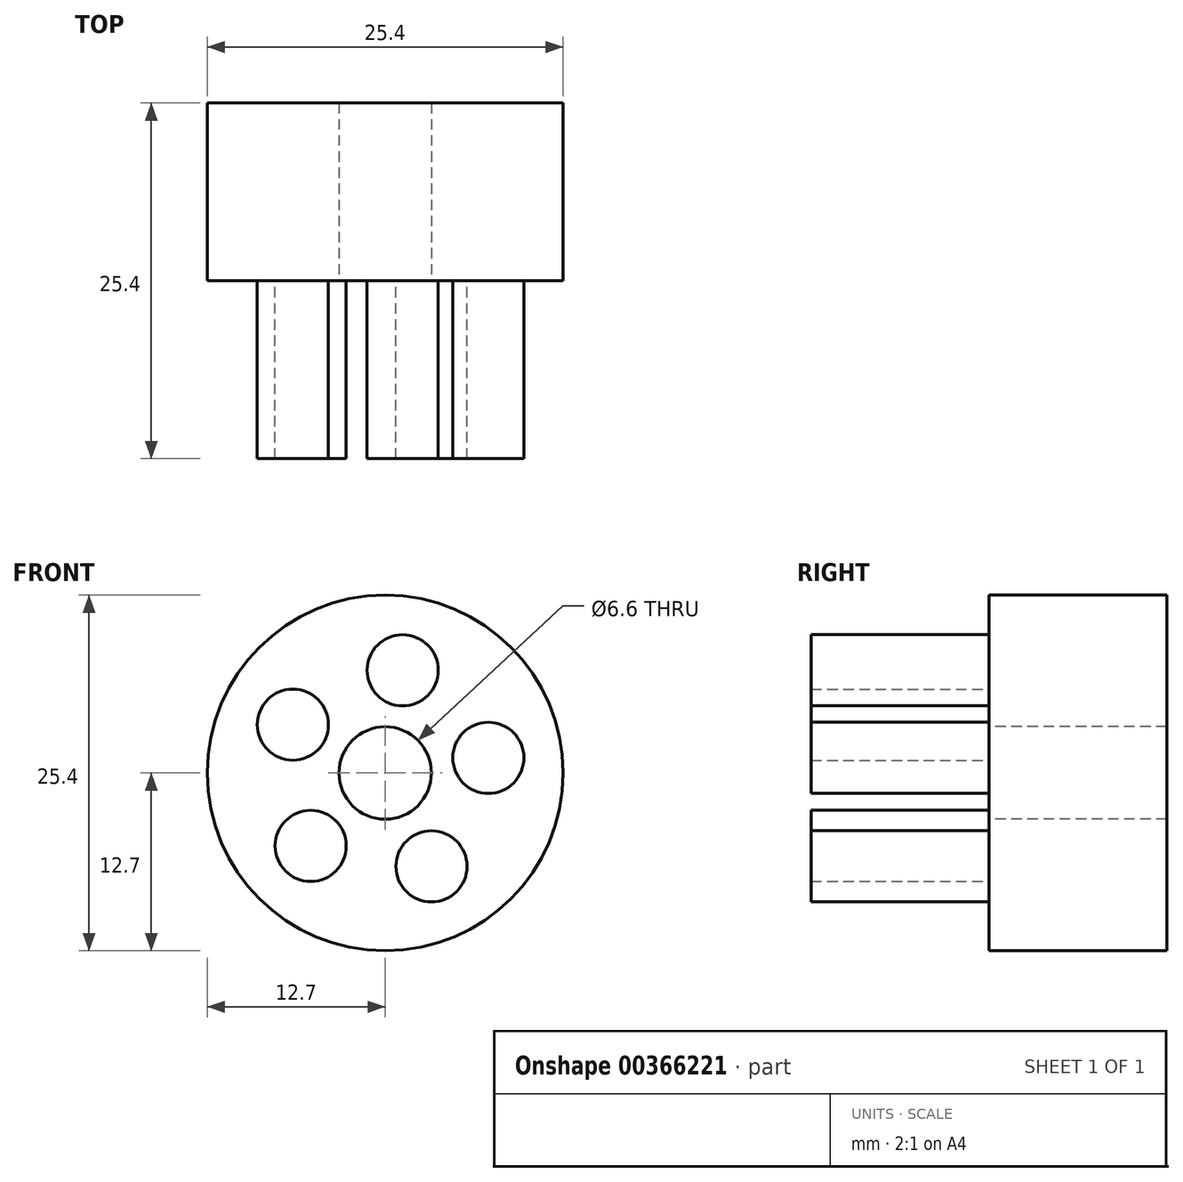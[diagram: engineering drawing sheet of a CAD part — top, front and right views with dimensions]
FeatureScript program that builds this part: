
annotation { "Feature Type Name" : "Feature", "Feature Type Description" : "" }
export const myFeature = defineFeature(function(context is Context, id is Id, definition is map)
    precondition{}
    {
        {
            var Q0;
            Q0=qCreatedBy(makeId("Front.planeOp"),FACE);
            var sketch = newSketch(context, id + "F0", { "sketchPlane" : qUnion([Q0])});
            skCircle(sketch, "E0", {"center": v(0, 0) * mm, "radius": 12.7 * mm});
            skSolve(sketch);
        }
        {
            var Q0;
            Q0 = qSketchRegion(id + "F0", true);
            var Q1;
            Q1=makeQuery(id+"F0.imprint","IMPRINT",FACE,{"disambiguationData":[TD([[makeQuery(id+"F0.imprint","IMPRINT",EDGE,{"derivedFrom":sQuery(id+"F0.wireOp",EDGE,"E0")}),1.0]])]});
            extrude(context, id + "F1", {"entities" : qUnion([Q0, Q1]), "depth" : 12.7 * mm});
        }
        {
            var Q0;
            Q0=makeQuery(id+"F1.opExtrude","CAP_FACE",FACE,{"disambiguationData":[OSD([sQuery(id+"F0.wireOp",EDGE,"E0")])],"isStart":false});
            var sketch = newSketch(context, id + "F2", { "sketchPlane" : qUnion([Q0])});
            skCircle(sketch, "E1", {"center": v(0, 0) * mm, "radius": 3.3 * mm});
            skSolve(sketch);
        }
        {
            var Q0;
            Q0=makeQuery(id+"F2.imprint","IMPRINT",FACE,{"disambiguationData":[TD([[makeQuery(id+"F2.imprint","IMPRINT",EDGE,{"derivedFrom":sQuery(id+"F2.wireOp",EDGE,"E1")}),1.0]])]});
            extrude(context, id + "F3", {"entities" : qUnion([Q0]), "operationType" : NewBodyOperationType.REMOVE, "oppositeDirection" : true, "depth" : 12.7 * mm});
        }
        {
            var Q0;
            Q0=makeQuery(id+"F1.opExtrude","CAP_FACE",FACE,{"disambiguationData":[OSD([sQuery(id+"F0.wireOp",EDGE,"E0")])],"isStart":false});
            var sketch = newSketch(context, id + "F4", { "sketchPlane" : qUnion([Q0])});
            skCircle(sketch, "E2", {"center": v(-6.6, 3.45) * mm, "radius": 2.54 * mm});
            skCircle(sketch, "E3.1.0", {"center": v(-5.32, -5.2) * mm, "radius": 2.54 * mm});
            skCircle(sketch, "E3.2.0", {"center": v(3.3, -6.67) * mm, "radius": 2.54 * mm});
            skCircle(sketch, "E3.3.0", {"center": v(7.36, 1.08) * mm, "radius": 2.54 * mm});
            skCircle(sketch, "E3.4.0", {"center": v(1.24, 7.34) * mm, "radius": 2.54 * mm});
            skPoint(sketch, "E3.center", {"position": v(0, 0) * mm});
            skSolve(sketch);
        }
        {
            var Q0;
            Q0=makeQuery(id+"F4.imprint","IMPRINT",FACE,{"disambiguationData":[TD([[makeQuery(id+"F4.imprint","IMPRINT",EDGE,{"derivedFrom":sQuery(id+"F4.wireOp",EDGE,"E3.4.0")}),1.0]])]});
            var Q1;
            Q1=makeQuery(id+"F4.imprint","IMPRINT",FACE,{"disambiguationData":[TD([[makeQuery(id+"F4.imprint","IMPRINT",EDGE,{"derivedFrom":sQuery(id+"F4.wireOp",EDGE,"E2")}),1.0]])]});
            var Q2;
            Q2=makeQuery(id+"F4.imprint","IMPRINT",FACE,{"disambiguationData":[TD([[makeQuery(id+"F4.imprint","IMPRINT",EDGE,{"derivedFrom":sQuery(id+"F4.wireOp",EDGE,"E3.1.0")}),1.0]])]});
            var Q3;
            Q3=makeQuery(id+"F4.imprint","IMPRINT",FACE,{"disambiguationData":[TD([[makeQuery(id+"F4.imprint","IMPRINT",EDGE,{"derivedFrom":sQuery(id+"F4.wireOp",EDGE,"E3.2.0")}),1.0]])]});
            var Q4;
            Q4=makeQuery(id+"F4.imprint","IMPRINT",FACE,{"disambiguationData":[TD([[makeQuery(id+"F4.imprint","IMPRINT",EDGE,{"derivedFrom":sQuery(id+"F4.wireOp",EDGE,"E3.3.0")}),1.0]])]});
            extrude(context, id + "F5", {"entities" : qUnion([Q0, Q1, Q2, Q3, Q4]), "operationType" : NewBodyOperationType.ADD, "depth" : 12.7 * mm});
        }
    });
